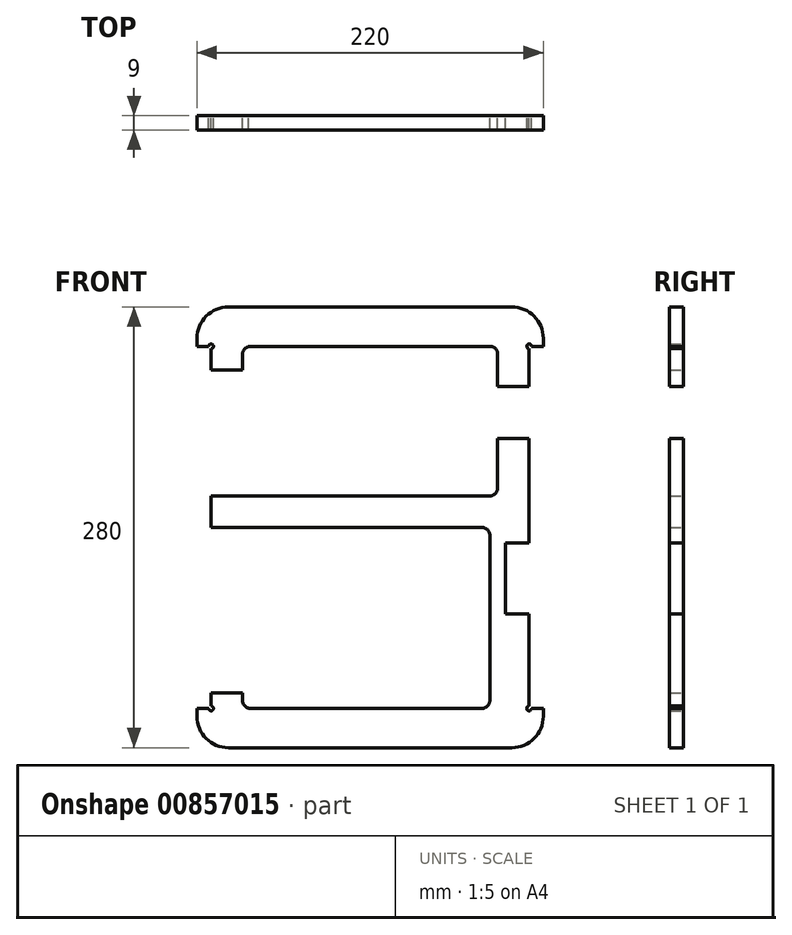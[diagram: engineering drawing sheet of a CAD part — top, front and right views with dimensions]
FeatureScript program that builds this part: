
annotation { "Feature Type Name" : "Feature", "Feature Type Description" : "" }
export const myFeature = defineFeature(function(context is Context, id is Id, definition is map)
    precondition{}
    {
        {
            var Q0;
            Q0=qCreatedBy(makeId("Front.planeOp"),FACE);
            var sketch = newSketch(context, id + "F0", { "sketchPlane" : qUnion([Q0])});
            skLineSegment(sketch, "E0.bottom", {"start": v(-90, 137.55) * mm, "end": v(90, 137.55) * mm});
            skLineSegment(sketch, "E0.top", {"start": v(-90, -142.45) * mm, "end": v(90, -142.45) * mm});
            skLineSegment(sketch, "E0.left", {"start": v(-110, 117.55) * mm, "end": v(-110, 112.55) * mm});
            skLineSegment(sketch, "E0.right", {"start": v(110, 117.55) * mm, "end": v(110, 112.55) * mm});
            skPoint(sketch, "E0.middle", {"position": v(0, -2.45) * mm});
            skLineSegment(sketch, "E1.bottom", {"start": v(-76, 17.55) * mm, "end": v(76, 17.55) * mm});
            skLineSegment(sketch, "E2", {"start": v(-110, 112.55) * mm, "end": v(-101, 112.55) * mm});
            skLineSegment(sketch, "E3", {"start": v(-110, -117.45) * mm, "end": v(-101, -117.45) * mm});
            skLineSegment(sketch, "E4.0", {"start": v(-101, 112.55) * mm, "end": v(-101, 97.55) * mm});
            skLineSegment(sketch, "E5.trimOffspring", {"start": v(-110, -117.45) * mm, "end": v(-110, -122.45) * mm});
            skLineSegment(sketch, "E6.0", {"start": v(-81, 107.55) * mm, "end": v(-81, 97.55) * mm});
            skLineSegment(sketch, "E7.0", {"start": v(81, 107.55) * mm, "end": v(81, 87.05) * mm});
            skLineSegment(sketch, "E8.trimOffspring", {"start": v(-76, 112.55) * mm, "end": v(76, 112.55) * mm});
            skLineSegment(sketch, "E9.trimOffspring", {"start": v(-76, -117.45) * mm, "end": v(71, -117.45) * mm});
            skLineSegment(sketch, "E10.trimOffspring", {"start": v(-76, -2.45) * mm, "end": v(71, -2.45) * mm});
            skPoint(sketch, "E11.visualSharp", {"position": v(-110, 137.55) * mm});
            skArc(sketch, "E11.filletArc", {"start": v(-90, 137.55) * mm, "mid": v(-104.14, 131.7) * mm, "end": v(-110, 117.55) * mm});
            skPoint(sketch, "E12.visualSharp", {"position": v(110, 137.55) * mm});
            skArc(sketch, "E12.filletArc", {"start": v(110, 117.55) * mm, "mid": v(104.14, 131.7) * mm, "end": v(90, 137.55) * mm});
            skPoint(sketch, "E13.visualSharp", {"position": v(110, -142.45) * mm});
            skArc(sketch, "E13.filletArc", {"start": v(90, -142.45) * mm, "mid": v(104.14, -136.6) * mm, "end": v(110, -122.45) * mm});
            skPoint(sketch, "E14.visualSharp", {"position": v(-110, -142.45) * mm});
            skArc(sketch, "E14.filletArc", {"start": v(-110, -122.45) * mm, "mid": v(-104.14, -136.6) * mm, "end": v(-90, -142.45) * mm});
            skLineSegment(sketch, "E15.trimOffspring", {"start": v(110, -117.45) * mm, "end": v(110, -122.45) * mm});
            skLineSegment(sketch, "E16.trimOffspring", {"start": v(101, -117.45) * mm, "end": v(110, -117.45) * mm});
            skLineSegment(sketch, "E17.trimOffspring", {"start": v(101, 112.55) * mm, "end": v(101, 87.05) * mm});
            skLineSegment(sketch, "E18.trimOffspring", {"start": v(101, 112.55) * mm, "end": v(110, 112.55) * mm});
            skPoint(sketch, "E19.visualSharp", {"position": v(81, 17.55) * mm});
            skArc(sketch, "E19.filletArc", {"start": v(76, 17.55) * mm, "mid": v(79.54, 19.02) * mm, "end": v(81, 22.55) * mm});
            skPoint(sketch, "E20.visualSharp", {"position": v(-81, 17.55) * mm});
            skPoint(sketch, "E21.visualSharp", {"position": v(-81, -2.45) * mm});
            skArc(sketch, "E21.filletArc", {"start": v(-76, -2.45) * mm, "mid": v(-76.65, -2.5) * mm, "end": v(-77.3, -2.62) * mm});
            skPoint(sketch, "E22.visualSharp", {"position": v(-81, -117.45) * mm});
            skArc(sketch, "E22.filletArc", {"start": v(-81, -112.45) * mm, "mid": v(-79.54, -115.98) * mm, "end": v(-76, -117.45) * mm});
            skPoint(sketch, "E23.visualSharp", {"position": v(-81, 112.55) * mm});
            skArc(sketch, "E23.filletArc", {"start": v(-76, 112.55) * mm, "mid": v(-79.54, 111.09) * mm, "end": v(-81, 107.55) * mm});
            skPoint(sketch, "E24.visualSharp", {"position": v(81, 112.55) * mm});
            skArc(sketch, "E24.filletArc", {"start": v(81, 107.55) * mm, "mid": v(79.54, 111.09) * mm, "end": v(76, 112.55) * mm});
            skCircle(sketch, "E25", {"center": v(-101, 112.55) * mm, "radius": 1.5 * mm});
            skCircle(sketch, "E26", {"center": v(101, 112.55) * mm, "radius": 1.5 * mm});
            skCircle(sketch, "E27", {"center": v(-101, -117.45) * mm, "radius": 1.5 * mm});
            skCircle(sketch, "E28", {"center": v(101, -117.45) * mm, "radius": 1.5 * mm});
            skLineSegment(sketch, "E29.bottom", {"start": v(-101, 97.55) * mm, "end": v(-81, 97.55) * mm});
            skLineSegment(sketch, "E29.top", {"start": v(-101, -107.45) * mm, "end": v(-81, -107.45) * mm});
            skLineSegment(sketch, "E29.right", {"start": v(101, 54.05) * mm, "end": v(101, -12.45) * mm});
            skLineSegment(sketch, "E30.trimOffspring", {"start": v(-101, 17.55) * mm, "end": v(-101, -2.62) * mm});
            skLineSegment(sketch, "E31.trimOffspring", {"start": v(-81, -107.45) * mm, "end": v(-81, -112.45) * mm});
            skLineSegment(sketch, "E32.trimOffspring", {"start": v(-101, -107.45) * mm, "end": v(-101, -117.45) * mm});
            skLineSegment(sketch, "E33.bottom", {"start": v(-76, 17.55) * mm, "end": v(-101, 17.55) * mm});
            skLineSegment(sketch, "E33.top", {"start": v(-76, -2.62) * mm, "end": v(-101, -2.62) * mm});
            skLineSegment(sketch, "E33.left", {"start": v(-76, -2.45) * mm, "end": v(-76, -2.62) * mm});
            skPoint(sketch, "E34", {"position": v(101, -57.45) * mm});
            skLineSegment(sketch, "E35", {"start": v(101, -57.45) * mm, "end": v(86, -57.45) * mm});
            skLineSegment(sketch, "E36", {"start": v(101, -12.45) * mm, "end": v(86, -12.45) * mm});
            skLineSegment(sketch, "E37", {"start": v(86, -57.45) * mm, "end": v(86, -12.45) * mm});
            skLineSegment(sketch, "E38.trimOffspring", {"start": v(101, -57.45) * mm, "end": v(101, -107.45) * mm});
            skLineSegment(sketch, "E39.trimOffspring", {"start": v(101, -57.45) * mm, "end": v(101, -117.45) * mm});
            skLineSegment(sketch, "E40", {"start": v(76, -7.45) * mm, "end": v(76, -33.11) * mm});
            skLineSegment(sketch, "E41", {"start": v(76, -33.11) * mm, "end": v(76, -112.45) * mm});
            skPoint(sketch, "E42.visualSharp", {"position": v(76, -2.45) * mm});
            skArc(sketch, "E42.filletArc", {"start": v(76, -7.45) * mm, "mid": v(74.54, -3.91) * mm, "end": v(71, -2.45) * mm});
            skPoint(sketch, "E43.visualSharp", {"position": v(76, -117.45) * mm});
            skArc(sketch, "E43.filletArc", {"start": v(71, -117.45) * mm, "mid": v(74.54, -115.98) * mm, "end": v(76, -112.45) * mm});
            skPoint(sketch, "E44", {"position": v(65.66, 87.05) * mm});
            skPoint(sketch, "E45", {"position": v(70.74, 54.05) * mm});
            skLineSegment(sketch, "E46", {"start": v(81, 87.05) * mm, "end": v(101, 87.05) * mm});
            skLineSegment(sketch, "E47", {"start": v(81, 54.05) * mm, "end": v(101, 54.05) * mm});
            skLineSegment(sketch, "E48.trimOffspring", {"start": v(81, 54.05) * mm, "end": v(81, 22.55) * mm});
            skPoint(sketch, "E49.orphan", {"position": v(101, 82.55) * mm});
            skSolve(sketch);
        }
        {
            var Q0;
            Q0=makeQuery(id+"F0.imprint","IMPRINT",FACE,{"disambiguationData":[TD([[makeQuery(id+"F0.imprint","IMPRINT",EDGE,{"derivedFrom":sQuery(id+"F0.wireOp",EDGE,"E0.bottom")}),-1.0]])]});
            var Q1;
            Q1=makeQuery(id+"F0.imprint","IMPRINT",FACE,{"disambiguationData":[TD([[makeQuery(id+"F0.imprint","IMPRINT",EDGE,{"derivedFrom":sQuery(id+"F0.wireOp",EDGE,"E0.top")}),1.0]])]});
            extrude(context, id + "F1", {"entities" : qUnion([Q0, Q1]), "depth" : 9 * mm, "offsetDistance" : 25 * mm});
        }
    });
